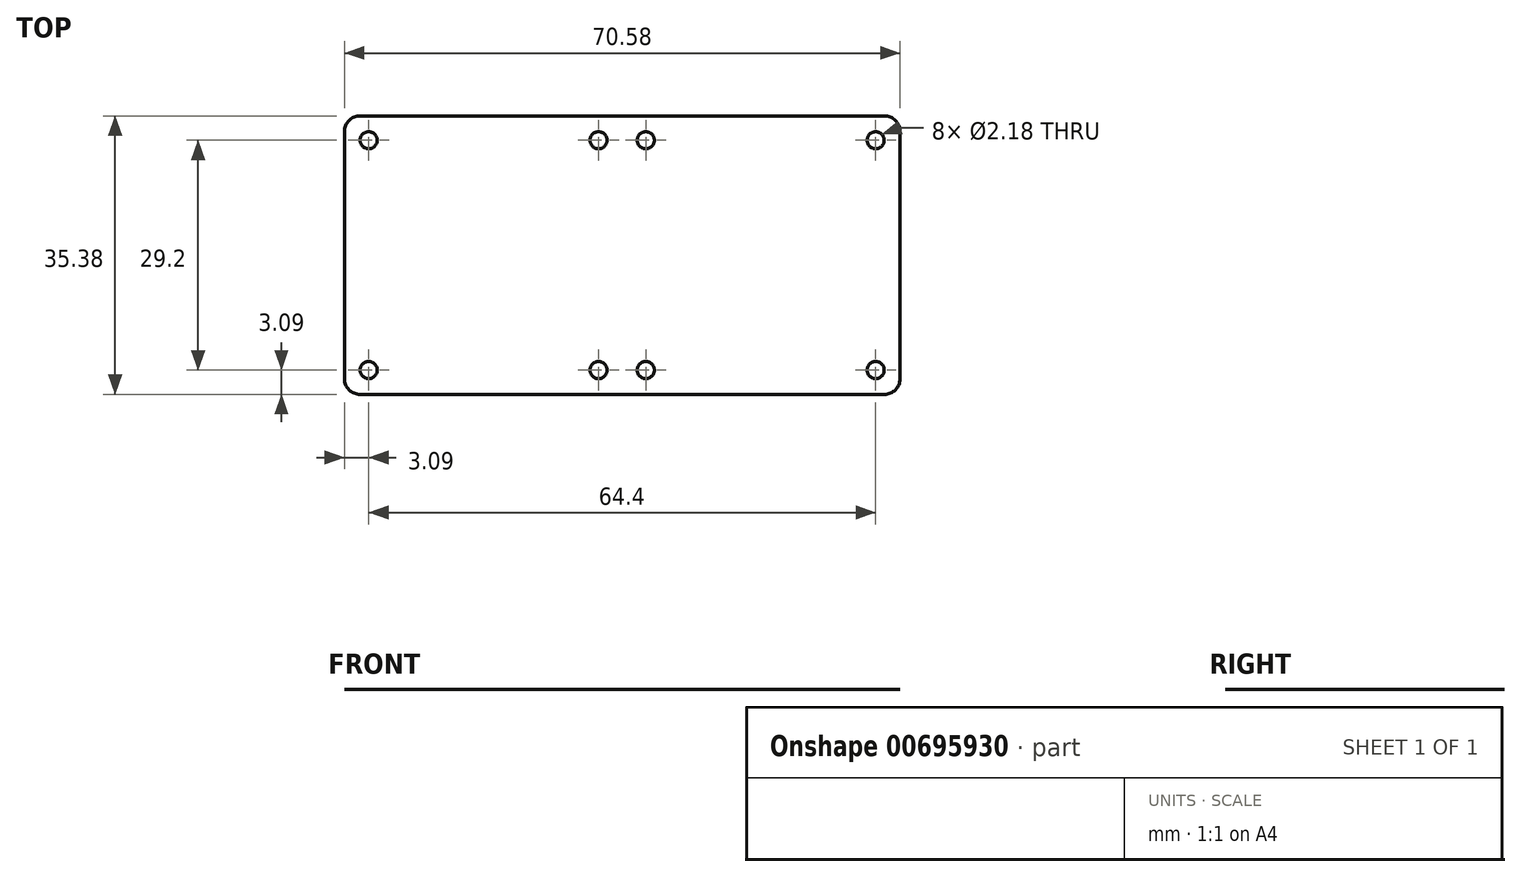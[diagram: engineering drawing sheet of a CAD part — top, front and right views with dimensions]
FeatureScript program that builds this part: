
annotation { "Feature Type Name" : "Feature", "Feature Type Description" : "" }
export const myFeature = defineFeature(function(context is Context, id is Id, definition is map)
    precondition{}
    {
        {
            var Q0;
            Q0=qCreatedBy(makeId("Top.planeOp"),FACE);
            var sketch = newSketch(context, id + "F0", { "sketchPlane" : qUnion([Q0])});
            skPoint(sketch, "E0.middle", {"position": v(-17.6, 0) * mm});
            skLineSegment(sketch, "E1.bottom", {"start": v(-3, -14.6) * mm, "end": v(-32.2, -14.6) * mm, "construction": true});
            skLineSegment(sketch, "E1.top", {"start": v(-3, 14.6) * mm, "end": v(-32.2, 14.6) * mm, "construction": true});
            skLineSegment(sketch, "E1.left", {"start": v(-3, -14.6) * mm, "end": v(-3, 14.6) * mm, "construction": true});
            skLineSegment(sketch, "E1.right", {"start": v(-32.2, -14.6) * mm, "end": v(-32.2, 14.6) * mm, "construction": true});
            skCircle(sketch, "E2", {"center": v(-3, 14.6) * mm, "radius": 1.09 * mm});
            skCircle(sketch, "E3", {"center": v(-3, -14.6) * mm, "radius": 1.09 * mm});
            skCircle(sketch, "E4", {"center": v(-32.2, -14.6) * mm, "radius": 1.09 * mm});
            skPoint(sketch, "E5.middle", {"position": v(17.6, 0) * mm});
            skLineSegment(sketch, "E6.bottom", {"start": v(32.2, -14.6) * mm, "end": v(3, -14.6) * mm, "construction": true});
            skLineSegment(sketch, "E6.top", {"start": v(32.2, 14.6) * mm, "end": v(3, 14.6) * mm, "construction": true});
            skLineSegment(sketch, "E6.left", {"start": v(32.2, -14.6) * mm, "end": v(32.2, 14.6) * mm, "construction": true});
            skLineSegment(sketch, "E6.right", {"start": v(3, -14.6) * mm, "end": v(3, 14.6) * mm, "construction": true});
            skCircle(sketch, "E7", {"center": v(32.2, 14.6) * mm, "radius": 1.09 * mm});
            skCircle(sketch, "E8", {"center": v(32.2, -14.6) * mm, "radius": 1.09 * mm});
            skCircle(sketch, "E9", {"center": v(3, -14.6) * mm, "radius": 1.09 * mm});
            skLineSegment(sketch, "E10", {"start": v(-17.6, 0) * mm, "end": v(17.6, 0) * mm, "construction": true});
            skCircle(sketch, "E11", {"center": v(-32.2, 14.6) * mm, "radius": 1.09 * mm});
            skCircle(sketch, "E12", {"center": v(3, 14.6) * mm, "radius": 1.09 * mm});
            skSolve(sketch);
        }
        {
            var Q0;
            Q0=qCreatedBy(makeId("Top.planeOp"),FACE);
            var sketch = newSketch(context, id + "F1", { "sketchPlane" : qUnion([Q0])});
            skLineSegment(sketch, "E13.bottom", {"start": v(35.3, -17.7) * mm, "end": v(-35.29, -17.7) * mm});
            skLineSegment(sketch, "E13.top", {"start": v(35.3, 17.7) * mm, "end": v(-35.29, 17.7) * mm});
            skLineSegment(sketch, "E13.left", {"start": v(35.29, -17.7) * mm, "end": v(35.29, 17.7) * mm});
            skLineSegment(sketch, "E13.right", {"start": v(-35.3, -17.7) * mm, "end": v(-35.3, 17.7) * mm});
            skPoint(sketch, "E13.middle", {"position": v(0, 0) * mm});
            skSolve(sketch);
        }
        {
            var Q0;
            Q0 = qSketchRegion(id + "F1", true);
            extrude(context, id + "F2", {"entities" : qUnion([Q0]), "depth" : 1 / 203.2 * mm, "offsetDistance" : 25 * mm});
        }
        {
            var Q0;
            Q0 = qSketchRegion(id + "F0", true);
            extrude(context, id + "F3", {"entities" : qUnion([Q0]), "operationType" : NewBodyOperationType.REMOVE, "endBound" : BoundingType.THROUGH_ALL, "depth" : 25 * mm, "offsetDistance" : 25 * mm});
        }
        {
            var Q0;
            Q0=makeQuery(id+"F2.opExtrude","SWEPT_EDGE",EDGE,{"disambiguationData":[OSD([sQuery(id+"F1.wireOp",EDGE,"E13.bottom"),sQuery(id+"F1.wireOp",EDGE,"E13.right")])]});
            var Q1;
            Q1=makeQuery(id+"F2.opExtrude","SWEPT_EDGE",EDGE,{"disambiguationData":[OSD([sQuery(id+"F1.wireOp",EDGE,"E13.top"),sQuery(id+"F1.wireOp",EDGE,"E13.right")])]});
            var Q2;
            Q2=makeQuery(id+"F2.opExtrude","SWEPT_EDGE",EDGE,{"disambiguationData":[OSD([sQuery(id+"F1.wireOp",EDGE,"E13.top"),sQuery(id+"F1.wireOp",EDGE,"E13.left")])]});
            var Q3;
            Q3=makeQuery(id+"F2.opExtrude","SWEPT_EDGE",EDGE,{"disambiguationData":[OSD([sQuery(id+"F1.wireOp",EDGE,"E13.bottom"),sQuery(id+"F1.wireOp",EDGE,"E13.left")])]});
            fillet(context, id + "F4", {"entities" : qUnion([Q0, Q1, Q2, Q3]), "radius" : 2 * mm, "tangentPropagation" : true, "allowEdgeOverflow" : false});
        }
    });
